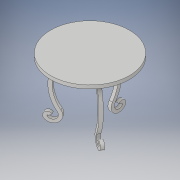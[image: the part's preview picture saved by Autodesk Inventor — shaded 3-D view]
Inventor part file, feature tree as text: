
AUTODESK INVENTOR PART (.ipt)
format: ipt  version: 2017 (Build 210142000, 142)  size: 207,872 bytes
history: native  units: in
note: dims shown in document units (in); Inventor stores cm internally (conversion verified against a paired STEP export)
features: sketch x2, extrude x1, pattern_circular x1, revolve x1
ambient origin geometry x8: Origin, YZ Plane, XZ Plane, XY Plane, X Axis, Y Axis, Z Axis, Center Point
bodies: Solid1 (feature_tree)
feature tree (5):
  extrude  "leg"  Depth=0.026in
  pattern_circular  "Circular Pattern1"  Count=3 Angle=360.0deg
  revolve  "Revolution1"  [1 undecoded]
  sketch  "Sketch1"  dims[d10=0.026in d11=0.026in d12=0.026in d15=0.026in]
  sketch  "Sketch2"  dims[d16=0.026in d17=0.0in d18=1.1811in d19=360.0deg d21=0.028in d22=0.119in d23=0.2in d24=90.0deg]
note: 1 required parameter value undecoded (feature->parameter linkage not recoverable at this tier; creation-order binding heuristic only, values carry confidence <= 0.55)
